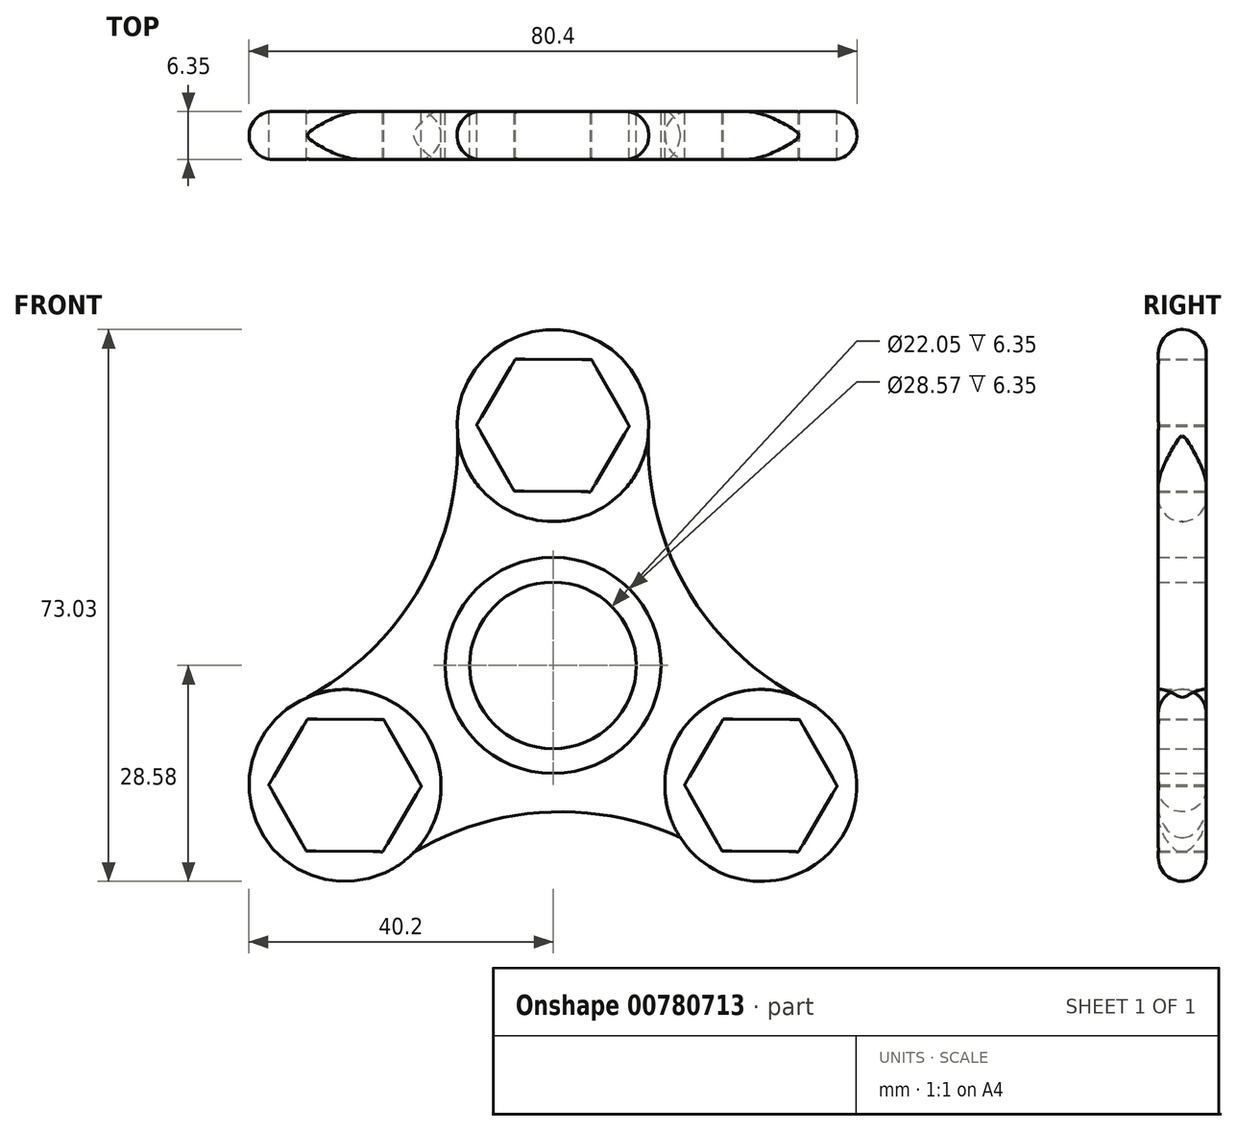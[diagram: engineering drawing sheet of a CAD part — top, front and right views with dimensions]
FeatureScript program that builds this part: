
annotation { "Feature Type Name" : "Feature", "Feature Type Description" : "" }
export const myFeature = defineFeature(function(context is Context, id is Id, definition is map)
    precondition{}
    {
        {
            var Q0;
            Q0=qCreatedBy(makeId("Front.planeOp"),FACE);
            var sketch = newSketch(context, id + "F0", { "sketchPlane" : qUnion([Q0])});
            skCircle(sketch, "E0", {"center": v(0, 0) * mm, "radius": 11.02 * mm});
            skCircle(sketch, "E1", {"center": v(0, 0) * mm, "radius": 14.29 * mm});
            skCircle(sketch, "E2.cCircle", {"center": v(0, 31.75) * mm, "radius": 8.74 * mm, "construction": true});
            skLineSegment(sketch, "E2.0", {"start": v(10.09, 31.67) * mm, "end": v(4.97, 22.97) * mm});
            skLineSegment(sketch, "E2.1", {"start": v(4.97, 22.97) * mm, "end": v(-5.12, 23.05) * mm});
            skLineSegment(sketch, "E2.2", {"start": v(-5.12, 23.05) * mm, "end": v(-10.09, 31.83) * mm});
            skLineSegment(sketch, "E2.3", {"start": v(-10.09, 31.83) * mm, "end": v(-4.97, 40.53) * mm});
            skLineSegment(sketch, "E2.4", {"start": v(-4.97, 40.53) * mm, "end": v(5.12, 40.45) * mm});
            skLineSegment(sketch, "E2.5", {"start": v(5.12, 40.45) * mm, "end": v(10.09, 31.67) * mm});
            skPoint(sketch, "E2.0.midPoint", {"position": v(7.53, 27.32) * mm});
            skCircle(sketch, "E3", {"center": v(0, 31.75) * mm, "radius": 12.7 * mm});
            skSolve(sketch);
        }
        {
            var Q0;
            Q0=qCreatedBy(makeId("Front.planeOp"),FACE);
            var sketch = newSketch(context, id + "F1", { "sketchPlane" : qUnion([Q0])});
            skCircle(sketch, "E4.0", {"center": v(0, 31.75) * mm, "radius": 8.74 * mm});
            skLineSegment(sketch, "E4.1", {"start": v(4.97, 22.97) * mm, "end": v(-5.12, 23.05) * mm});
            skLineSegment(sketch, "E4.2", {"start": v(-5.12, 23.05) * mm, "end": v(-10.09, 31.83) * mm});
            skLineSegment(sketch, "E4.3", {"start": v(-10.09, 31.83) * mm, "end": v(-4.97, 40.53) * mm});
            skLineSegment(sketch, "E4.4", {"start": v(-4.97, 40.53) * mm, "end": v(5.12, 40.45) * mm});
            skLineSegment(sketch, "E4.5", {"start": v(5.12, 40.45) * mm, "end": v(10.09, 31.67) * mm});
            skCircle(sketch, "E4.6", {"center": v(0, 31.75) * mm, "radius": 12.7 * mm});
            skLineSegment(sketch, "E4.7", {"start": v(10.09, 31.67) * mm, "end": v(4.97, 22.97) * mm});
            skCircle(sketch, "E5.1.0", {"center": v(-27.5, -15.87) * mm, "radius": 8.74 * mm});
            skLineSegment(sketch, "E5.1.1", {"start": v(-22.38, -7.18) * mm, "end": v(-17.4, -15.96) * mm});
            skLineSegment(sketch, "E5.1.2", {"start": v(-17.4, -15.96) * mm, "end": v(-22.52, -24.65) * mm});
            skLineSegment(sketch, "E5.1.3", {"start": v(-22.52, -24.65) * mm, "end": v(-32.61, -24.57) * mm});
            skLineSegment(sketch, "E5.1.4", {"start": v(-32.61, -24.57) * mm, "end": v(-37.59, -15.8) * mm});
            skLineSegment(sketch, "E5.1.5", {"start": v(-37.59, -15.8) * mm, "end": v(-32.47, -7.1) * mm});
            skCircle(sketch, "E5.1.6", {"center": v(-27.5, -15.87) * mm, "radius": 12.7 * mm});
            skLineSegment(sketch, "E5.1.7", {"start": v(-32.47, -7.1) * mm, "end": v(-22.38, -7.18) * mm});
            skCircle(sketch, "E5.2.0", {"center": v(27.5, -15.88) * mm, "radius": 8.74 * mm});
            skLineSegment(sketch, "E5.2.1", {"start": v(17.4, -15.8) * mm, "end": v(22.52, -7.1) * mm});
            skLineSegment(sketch, "E5.2.2", {"start": v(22.52, -7.1) * mm, "end": v(32.61, -7.18) * mm});
            skLineSegment(sketch, "E5.2.3", {"start": v(32.61, -7.18) * mm, "end": v(37.59, -15.96) * mm});
            skLineSegment(sketch, "E5.2.4", {"start": v(37.59, -15.96) * mm, "end": v(32.47, -24.65) * mm});
            skLineSegment(sketch, "E5.2.5", {"start": v(32.47, -24.65) * mm, "end": v(22.38, -24.57) * mm});
            skCircle(sketch, "E5.2.6", {"center": v(27.5, -15.88) * mm, "radius": 12.7 * mm});
            skLineSegment(sketch, "E5.2.7", {"start": v(22.38, -24.57) * mm, "end": v(17.4, -15.8) * mm});
            skPoint(sketch, "E5.center", {"position": v(0, 0) * mm});
            skSolve(sketch);
        }
        {
            var Q0;
            Q0=qCreatedBy(makeId("Front.planeOp"),FACE);
            var sketch = newSketch(context, id + "F2", { "sketchPlane" : qUnion([Q0])});
            skCircle(sketch, "E6.0", {"center": v(0, 0) * mm, "radius": 11.02 * mm});
            skCircle(sketch, "E6.1", {"center": v(0, 0) * mm, "radius": 14.29 * mm});
            skLineSegment(sketch, "E6.2", {"start": v(4.97, 22.97) * mm, "end": v(-5.12, 23.05) * mm});
            skCircle(sketch, "E6.3", {"center": v(0, 31.75) * mm, "radius": 8.74 * mm});
            skCircle(sketch, "E6.4", {"center": v(-27.5, -15.87) * mm, "radius": 12.7 * mm});
            skLineSegment(sketch, "E6.5", {"start": v(-37.59, -15.8) * mm, "end": v(-32.47, -7.1) * mm});
            skCircle(sketch, "E6.6", {"center": v(27.5, -15.88) * mm, "radius": 8.74 * mm});
            skLineSegment(sketch, "E6.7", {"start": v(22.38, -24.57) * mm, "end": v(17.4, -15.8) * mm});
            skLineSegment(sketch, "E6.8", {"start": v(-5.12, 23.05) * mm, "end": v(-10.09, 31.83) * mm});
            skLineSegment(sketch, "E6.9", {"start": v(-10.09, 31.83) * mm, "end": v(-4.97, 40.53) * mm});
            skCircle(sketch, "E6.10", {"center": v(0, 31.75) * mm, "radius": 12.7 * mm});
            skCircle(sketch, "E6.11", {"center": v(-27.5, -15.87) * mm, "radius": 8.74 * mm});
            skLineSegment(sketch, "E6.12", {"start": v(-22.38, -7.18) * mm, "end": v(-17.4, -15.96) * mm});
            skLineSegment(sketch, "E6.13", {"start": v(-17.4, -15.96) * mm, "end": v(-22.52, -24.65) * mm});
            skLineSegment(sketch, "E6.14", {"start": v(17.4, -15.8) * mm, "end": v(22.52, -7.1) * mm});
            skLineSegment(sketch, "E6.15", {"start": v(-32.61, -24.57) * mm, "end": v(-37.59, -15.8) * mm});
            skCircle(sketch, "E6.16", {"center": v(27.5, -15.88) * mm, "radius": 12.7 * mm});
            skLineSegment(sketch, "E6.17", {"start": v(22.52, -7.1) * mm, "end": v(32.61, -7.18) * mm});
            skCircle(sketch, "E6.18", {"center": v(0, 31.75) * mm, "radius": 8.74 * mm});
            skLineSegment(sketch, "E6.19", {"start": v(10.09, 31.67) * mm, "end": v(4.97, 22.97) * mm});
            skLineSegment(sketch, "E6.20", {"start": v(4.97, 22.97) * mm, "end": v(-5.12, 23.05) * mm});
            skLineSegment(sketch, "E6.21", {"start": v(-5.12, 23.05) * mm, "end": v(-10.09, 31.83) * mm});
            skLineSegment(sketch, "E6.22", {"start": v(-10.09, 31.83) * mm, "end": v(-4.97, 40.53) * mm});
            skLineSegment(sketch, "E6.23", {"start": v(-4.97, 40.53) * mm, "end": v(5.12, 40.45) * mm});
            skLineSegment(sketch, "E6.24", {"start": v(5.12, 40.45) * mm, "end": v(10.09, 31.67) * mm});
            skCircle(sketch, "E6.25", {"center": v(0, 31.75) * mm, "radius": 12.7 * mm});
            skLineSegment(sketch, "E6.26", {"start": v(32.47, -24.65) * mm, "end": v(22.38, -24.57) * mm});
            skLineSegment(sketch, "E6.27", {"start": v(-22.52, -24.65) * mm, "end": v(-32.61, -24.57) * mm});
            skArc(sketch, "E7", {"start": v(-32.47, -4.19) * mm, "mid": v(-17.27, 10.9) * mm, "end": v(-12.7, 31.83) * mm});
            skArc(sketch, "E8", {"start": v(12.7, 31.83) * mm, "mid": v(17.69, 10.17) * mm, "end": v(33.98, -4.96) * mm});
            skArc(sketch, "E9", {"start": v(25.67, -28.44) * mm, "mid": v(1.81, -19.36) * mm, "end": v(-22.38, -27.5) * mm});
            skLineSegment(sketch, "E10.14", {"start": v(32.61, -7.18) * mm, "end": v(37.59, -15.96) * mm});
            skSolve(sketch);
        }
        {
            var Q0;
            Q0=qCreatedBy(makeId("Front.planeOp"),FACE);
            var sketch = newSketch(context, id + "F3", { "sketchPlane" : qUnion([Q0])});
            skSolve(sketch);
        }
        {
            var Q0;
            Q0 = qSketchRegion(id + "F3", true);
            var Q1;
            Q1=makeQuery(id+"F1.imprint","IMPRINT",FACE,{"disambiguationData":[TD([[makeQuery(id+"F1.imprint","IMPRINT",EDGE,{"derivedFrom":sQuery(id+"F1.wireOp",EDGE,"E5.1.6")}),1.0]])]});
            var Q2;
            Q2=makeQuery(id+"F1.imprint","IMPRINT",FACE,{"disambiguationData":[TD([[makeQuery(id+"F1.imprint","IMPRINT",EDGE,{"derivedFrom":sQuery(id+"F1.wireOp",EDGE,"E5.2.6")}),1.0]])]});
            var Q3;
            Q3=makeQuery(id+"F2.imprint","IMPRINT",FACE,{"disambiguationData":[TD([[makeQuery(id+"F2.imprint","IMPRINT",EDGE,{"derivedFrom":sQuery(id+"F2.wireOp",EDGE,"E6.1")}),-1.0]])]});
            var Q4;
            Q4=makeQuery(id+"F0.imprint","IMPRINT",FACE,{"disambiguationData":[TD([[makeQuery(id+"F0.imprint","IMPRINT",EDGE,{"derivedFrom":sQuery(id+"F0.wireOp",EDGE,"E2.0")}),1.0]])]});
            var Q5;
            Q5=makeQuery(id+"F0.imprint","IMPRINT",FACE,{"disambiguationData":[TD([[makeQuery(id+"F0.imprint","IMPRINT",EDGE,{"derivedFrom":sQuery(id+"F0.wireOp",EDGE,"E0")}),-1.0]])]});
            extrude(context, id + "F4", {"entities" : qUnion([Q0, Q1, Q2, Q3, Q4, Q5]), "depth" : 6.35 * mm, "offsetDistance" : 25.4 * mm});
        }
        {
            var Q0;
            Q0=makeQuery(id+"F4.opExtrude","CAP_EDGE",EDGE,{"disambiguationData":[OSD([sQuery(id+"F2.wireOp",EDGE,"E7")])],"isStart":false});
            var Q1;
            Q1=makeQuery(id+"F4.opExtrude","CAP_EDGE",EDGE,{"disambiguationData":[OSD([sQuery(id+"F1.wireOp",EDGE,"E5.1.6")])],"isStart":false});
            var Q2;
            Q2=makeQuery(id+"F4.opExtrude","CAP_EDGE",EDGE,{"disambiguationData":[OSD([sQuery(id+"F2.wireOp",EDGE,"E9")])],"isStart":false});
            var Q3;
            Q3=makeQuery(id+"F4.opExtrude","CAP_EDGE",EDGE,{"disambiguationData":[OSD([sQuery(id+"F1.wireOp",EDGE,"E5.2.6")])],"isStart":false});
            var Q4;
            Q4=makeQuery(id+"F4.opExtrude","CAP_EDGE",EDGE,{"disambiguationData":[OSD([sQuery(id+"F2.wireOp",EDGE,"E8")])],"isStart":false});
            var Q5;
            Q5=makeQuery(id+"F4.opExtrude","CAP_EDGE",EDGE,{"disambiguationData":[OSD([sQuery(id+"F0.wireOp",EDGE,"E3")])],"isStart":false});
            fillet(context, id + "F5", {"entities" : qUnion([Q0, Q1, Q2, Q3, Q4, Q5]), "radius" : 3.17 * mm, "tangentPropagation" : true, "allowEdgeOverflow" : false});
        }
        {
            var Q0;
            Q0=makeQuery(id+"F4.opExtrude","CAP_EDGE",EDGE,{"disambiguationData":[OSD([sQuery(id+"F2.wireOp",EDGE,"E8")])],"isStart":true});
            var Q1;
            Q1=makeQuery(id+"F4.opExtrude","CAP_EDGE",EDGE,{"disambiguationData":[OSD([sQuery(id+"F1.wireOp",EDGE,"E5.2.6")])],"isStart":true});
            var Q2;
            Q2=makeQuery(id+"F4.opExtrude","CAP_EDGE",EDGE,{"disambiguationData":[OSD([sQuery(id+"F2.wireOp",EDGE,"E9")])],"isStart":true});
            var Q3;
            Q3=makeQuery(id+"F4.opExtrude","CAP_EDGE",EDGE,{"disambiguationData":[OSD([sQuery(id+"F1.wireOp",EDGE,"E5.1.6")])],"isStart":true});
            var Q4;
            Q4=makeQuery(id+"F4.opExtrude","CAP_EDGE",EDGE,{"disambiguationData":[OSD([sQuery(id+"F2.wireOp",EDGE,"E7")])],"isStart":true});
            var Q5;
            Q5=makeQuery(id+"F4.opExtrude","CAP_EDGE",EDGE,{"disambiguationData":[OSD([sQuery(id+"F0.wireOp",EDGE,"E3")])],"isStart":true});
            fillet(context, id + "F6", {"entities" : qUnion([Q0, Q1, Q2, Q3, Q4, Q5]), "radius" : 3.17 * mm, "tangentPropagation" : true, "allowEdgeOverflow" : false});
        }
    });
